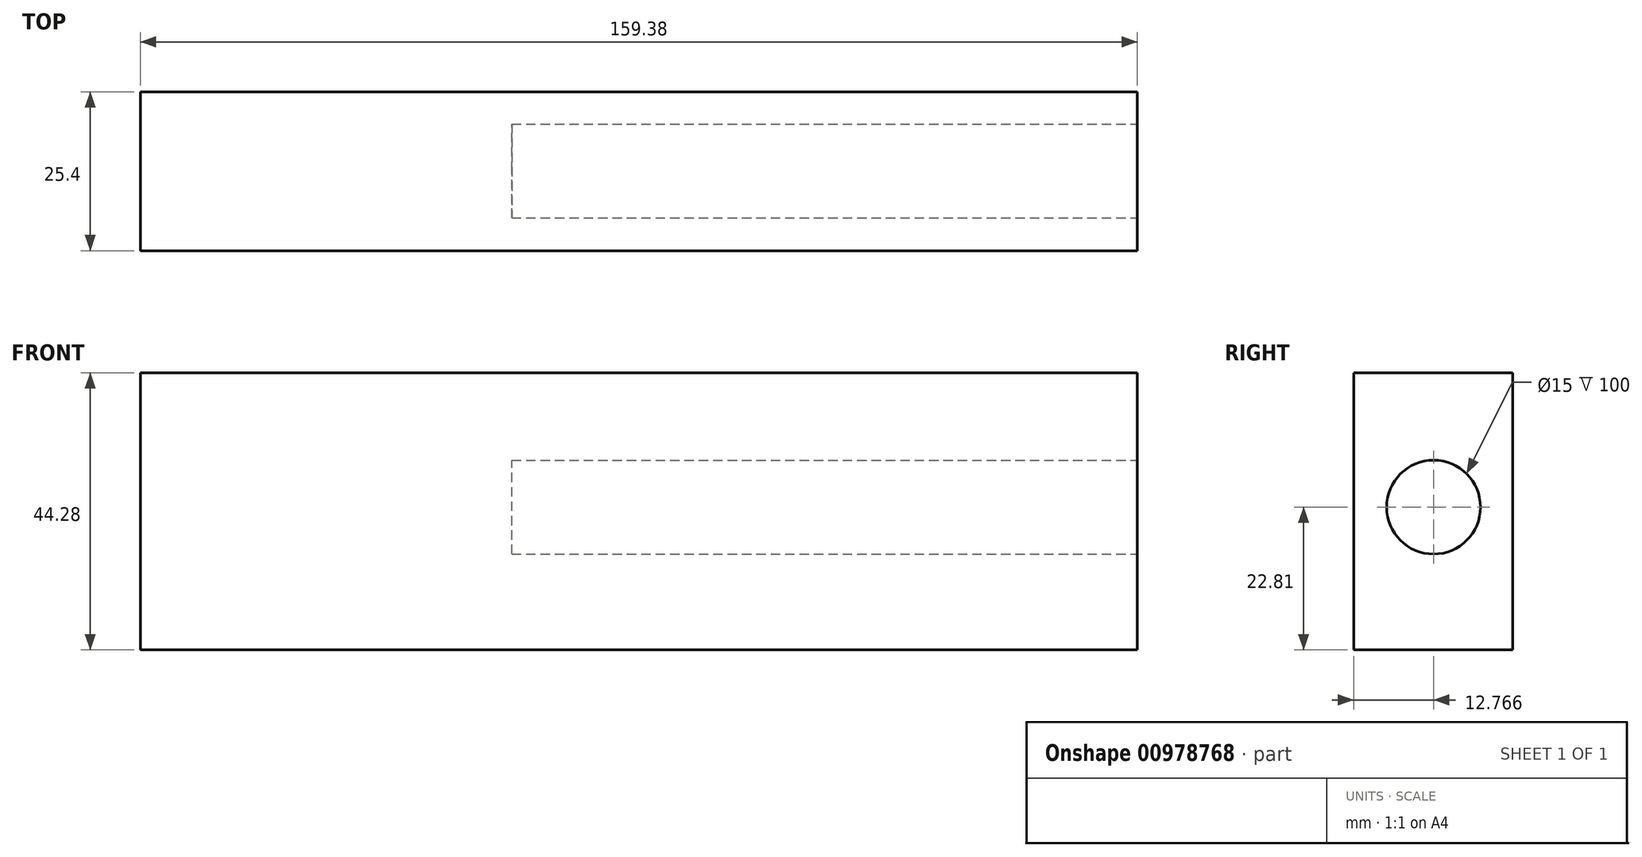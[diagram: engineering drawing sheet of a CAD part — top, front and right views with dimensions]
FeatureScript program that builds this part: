
annotation { "Feature Type Name" : "Feature", "Feature Type Description" : "" }
export const myFeature = defineFeature(function(context is Context, id is Id, definition is map)
    precondition{}
    {
        {
            var Q0;
            Q0=qCreatedBy(makeId("Front.planeOp"),FACE);
            var sketch = newSketch(context, id + "F0", { "sketchPlane" : qUnion([Q0])});
            skLineSegment(sketch, "E0.bottom", {"start": v(-29.69, 21.47) * mm, "end": v(29.69, 21.47) * mm});
            skLineSegment(sketch, "E0.top", {"start": v(-29.69, -22.81) * mm, "end": v(29.69, -22.81) * mm});
            skLineSegment(sketch, "E0.left", {"start": v(-29.69, 21.47) * mm, "end": v(-29.69, -22.81) * mm});
            skLineSegment(sketch, "E0.right", {"start": v(29.69, 21.47) * mm, "end": v(29.69, -22.81) * mm});
            skSolve(sketch);
        }
        {
            var Q0;
            Q0 = qSketchRegion(id + "F0", true);
            extrude(context, id + "F1", {"entities" : qUnion([Q0]), "depth" : 25.4 * mm, "offsetDistance" : 25.4 * mm});
        }
        {
            var Q0;
            Q0=makeQuery(id+"F1.opExtrude","SWEPT_FACE",FACE,{"disambiguationData":[OSD([sQuery(id+"F0.wireOp",EDGE,"E0.left")])]});
            extrude(context, id + "F2", {"entities" : qUnion([Q0]), "operationType" : NewBodyOperationType.ADD, "depth" : 100 * mm, "offsetDistance" : 25 * mm});
        }
        {
            var Q0;
            Q0=makeQuery(id+"F1.opExtrude","SWEPT_FACE",FACE,{"disambiguationData":[OSD([sQuery(id+"F0.wireOp",EDGE,"E0.right")])]});
            var sketch = newSketch(context, id + "F3", { "sketchPlane" : qUnion([Q0])});
            skCircle(sketch, "E1", {"center": v(-12.63, 0) * mm, "radius": 7.5 * mm});
            skSolve(sketch);
        }
        {
            var Q0;
            Q0=makeQuery(id+"F3.imprint","IMPRINT",FACE,{"disambiguationData":[TD([[makeQuery(id+"F3.imprint","IMPRINT",EDGE,{"derivedFrom":sQuery(id+"F3.wireOp",EDGE,"E1")}),1.0]])]});
            extrude(context, id + "F4", {"entities" : qUnion([Q0]), "operationType" : NewBodyOperationType.REMOVE, "oppositeDirection" : true, "depth" : 100 * mm, "offsetDistance" : 25 * mm});
        }
    });
